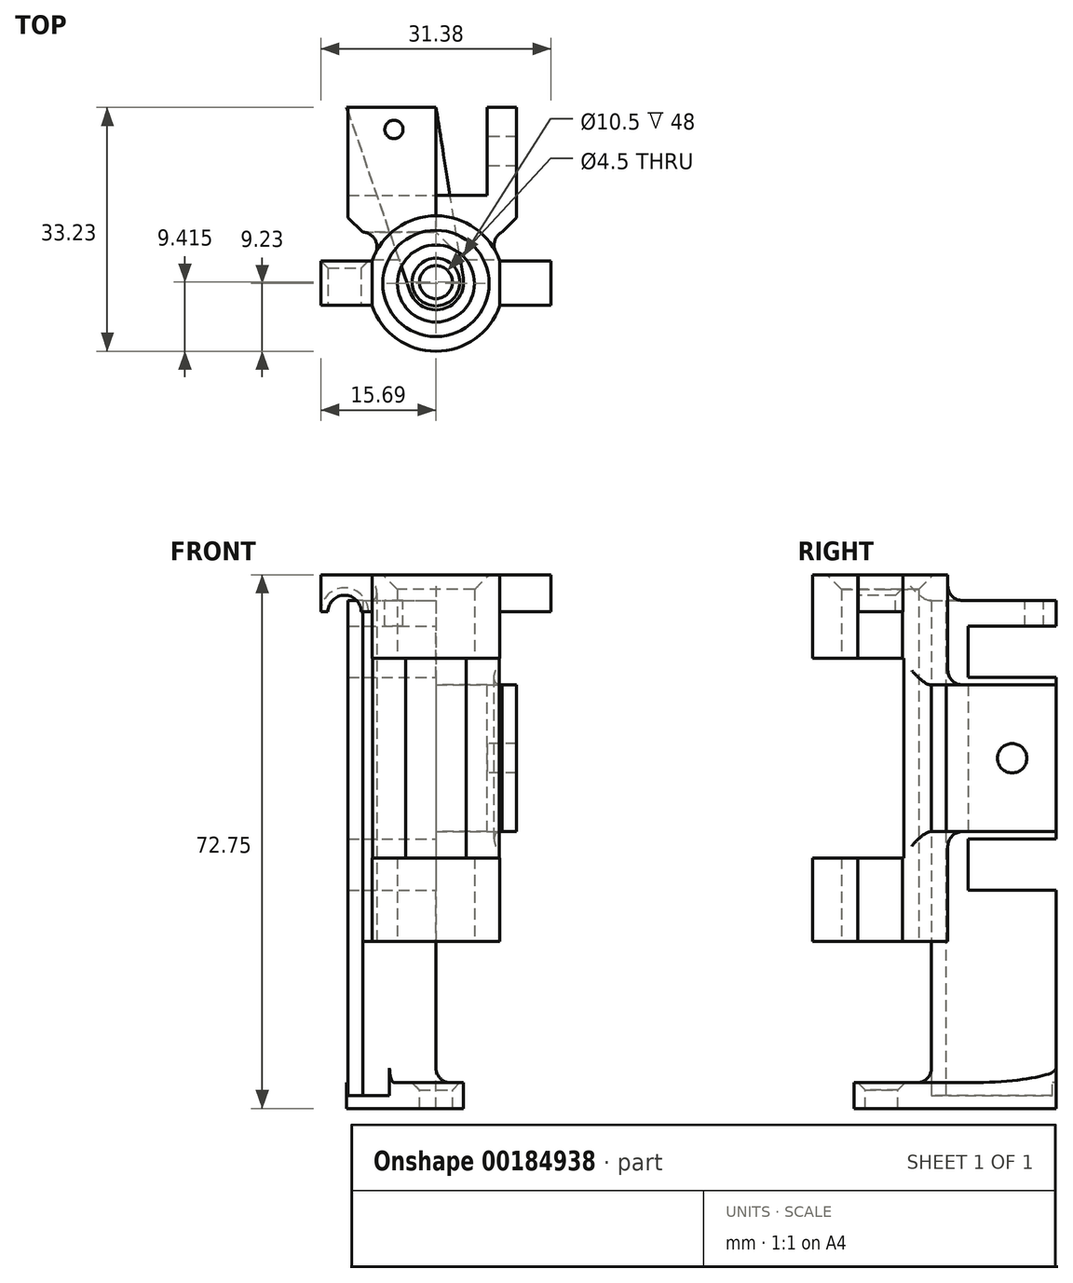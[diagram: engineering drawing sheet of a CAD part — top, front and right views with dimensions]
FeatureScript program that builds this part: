
annotation { "Feature Type Name" : "Feature", "Feature Type Description" : "" }
export const myFeature = defineFeature(function(context is Context, id is Id, definition is map)
    precondition{}
    {
        {
            var Q0;
            Q0=qCreatedBy(makeId("Front.planeOp"),FACE);
            var sketch = newSketch(context, id + "F0", { "sketchPlane" : qUnion([Q0])});
            skLineSegment(sketch, "E0", {"start": v(-12, 18) * mm, "end": v(-12, 11) * mm});
            skLineSegment(sketch, "E1", {"start": v(-12, 11) * mm, "end": v(0, 11) * mm});
            skLineSegment(sketch, "E2", {"start": v(0, 11) * mm, "end": v(0, 0) * mm});
            skLineSegment(sketch, "E3", {"start": v(-12, 18) * mm, "end": v(7, 18) * mm});
            skLineSegment(sketch, "E4", {"start": v(7, 18) * mm, "end": v(7, 0) * mm});
            skLineSegment(sketch, "E5.MirrorCS", {"start": v(0, -11) * mm, "end": v(0, 0) * mm});
            skLineSegment(sketch, "E6.MirrorCS", {"start": v(-12, -11) * mm, "end": v(0, -11) * mm});
            skLineSegment(sketch, "E7.MirrorCS", {"start": v(-12, -18) * mm, "end": v(-12, -11) * mm});
            skLineSegment(sketch, "E8.MirrorCS", {"start": v(-12, -18) * mm, "end": v(7, -18) * mm});
            skLineSegment(sketch, "E9.MirrorCS", {"start": v(7, -18) * mm, "end": v(7, 0) * mm});
            skSolve(sketch);
        }
        {
            var Q0;
            Q0=makeQuery(id+"F0.imprint","IMPRINT",FACE,{"disambiguationData":[TD([[makeQuery(id+"F0.imprint","IMPRINT",EDGE,{"derivedFrom":sQuery(id+"F0.wireOp",EDGE,"E0")}),1.0]])]});
            extrude(context, id + "F1", {"entities" : qUnion([Q0]), "depth" : 12 * mm});
        }
        {
            var Q0;
            Q0=qCreatedBy(makeId("Front.planeOp"),FACE);
            cPlane(context, id + "F2", {"entities" : qUnion([Q0]), "cplaneType" : CPlaneType.OFFSET, "offset" : 17 * mm, "width" : 150 * mm, "height" : 150 * mm});
        }
        {
            var Q0;
            Q0=qCreatedBy(id+"F2.planeOp",FACE);
            var sketch = newSketch(context, id + "F3", { "sketchPlane" : qUnion([Q0])});
            skLineSegment(sketch, "E10.bottom", {"start": v(-12, 21.5) * mm, "end": v(0, 21.5) * mm});
            skLineSegment(sketch, "E10.left", {"start": v(-12, 21.5) * mm, "end": v(-12, -27.5) * mm});
            skLineSegment(sketch, "E10.right", {"start": v(0, 21.5) * mm, "end": v(0, 10) * mm});
            skLineSegment(sketch, "E11", {"start": v(0, 10) * mm, "end": v(11, 10) * mm});
            skLineSegment(sketch, "E12", {"start": v(11, 10) * mm, "end": v(11, 0) * mm});
            skLineSegment(sketch, "E13.MirrorCS", {"start": v(0, -10) * mm, "end": v(11, -10) * mm});
            skLineSegment(sketch, "E14.MirrorCS", {"start": v(11, -10) * mm, "end": v(11, 0) * mm});
            skLineSegment(sketch, "E15.trimOffspring", {"start": v(0, -10) * mm, "end": v(0, -21.5) * mm});
            skLineSegment(sketch, "E16", {"start": v(-12, -27.5) * mm, "end": v(-12, -46) * mm});
            skLineSegment(sketch, "E17", {"start": v(-12, -46) * mm, "end": v(0, -46) * mm});
            skLineSegment(sketch, "E18", {"start": v(0, -46) * mm, "end": v(0, -21.5) * mm});
            skSolve(sketch);
        }
        {
            var Q0;
            Q0=makeQuery(id+"F3.imprint","IMPRINT",FACE,{"disambiguationData":[TD([[makeQuery(id+"F3.imprint","IMPRINT",EDGE,{"derivedFrom":sQuery(id+"F3.wireOp",EDGE,"E10.bottom")}),-1.0]])]});
            extrude(context, id + "F4", {"entities" : qUnion([Q0]), "oppositeDirection" : true, "depth" : 17 * mm});
        }
        {
            var Q0;
            Q0=makeQuery(id+"F1.opExtrude","SWEPT_BODY",BODY,{"disambiguationData":[OSD([sQuery(id+"F0.wireOp",EDGE,"E0"),sQuery(id+"F0.wireOp",EDGE,"E1"),sQuery(id+"F0.wireOp",EDGE,"E2"),sQuery(id+"F0.wireOp",EDGE,"E3"),sQuery(id+"F0.wireOp",EDGE,"E4"),sQuery(id+"F0.wireOp",EDGE,"E5.MirrorCS"),sQuery(id+"F0.wireOp",EDGE,"E6.MirrorCS"),sQuery(id+"F0.wireOp",EDGE,"E7.MirrorCS"),sQuery(id+"F0.wireOp",EDGE,"E8.MirrorCS"),sQuery(id+"F0.wireOp",EDGE,"E9.MirrorCS")])]});
            var Q1;
            Q1=makeQuery(id+"F4.opExtrude","SWEPT_BODY",BODY,{"disambiguationData":[OSD([sQuery(id+"F3.wireOp",EDGE,"E10.bottom"),sQuery(id+"F3.wireOp",EDGE,"E10.top"),sQuery(id+"F3.wireOp",EDGE,"E10.left"),sQuery(id+"F3.wireOp",EDGE,"E10.right"),sQuery(id+"F3.wireOp",EDGE,"E11"),sQuery(id+"F3.wireOp",EDGE,"E12"),sQuery(id+"F3.wireOp",EDGE,"E13.MirrorCS"),sQuery(id+"F3.wireOp",EDGE,"E14.MirrorCS"),sQuery(id+"F3.wireOp",EDGE,"E15.trimOffspring")])]});
            booleanBodies(context, id + "F5", {"operationType" : BooleanOperationType.SUBTRACTION, "tools" : qUnion([Q0]), "targets" : qUnion([Q1])});
        }
        {
            var Q0;
            Q0=qCreatedBy(makeId("Right.planeOp"),FACE);
            var sketch = newSketch(context, id + "F6", { "sketchPlane" : qUnion([Q0])});
            skCircle(sketch, "E19", {"center": v(-6, 0) * mm, "radius": 2 * mm});
            skSolve(sketch);
        }
        {
            var Q0;
            Q0 = qSketchRegion(id + "F6", true);
            extrude(context, id + "F7", {"entities" : qUnion([Q0]), "operationType" : NewBodyOperationType.REMOVE, "endBound" : BoundingType.THROUGH_ALL, "depth" : 25 * mm});
        }
        {
            var Q0;
            Q0=qCreatedBy(makeId("Top.planeOp"),FACE);
            var sketch = newSketch(context, id + "F8", { "sketchPlane" : qUnion([Q0])});
            skCircle(sketch, "E20", {"center": v(0, -24) * mm, "radius": 5.25 * mm});
            skArc(sketch, "E21", {"start": v(8.7, -20.95) * mm, "mid": v(0, -14.77) * mm, "end": v(-8.7, -20.95) * mm});
            skArc(sketch, "E22.trimOffspring", {"start": v(-8.7, -27.05) * mm, "mid": v(0, -33.23) * mm, "end": v(8.7, -27.05) * mm});
            skLineSegment(sketch, "E23", {"start": v(-8.7, -20.95) * mm, "end": v(-8.7, -27.05) * mm});
            skLineSegment(sketch, "E24.MirrorCS", {"start": v(8.7, -20.95) * mm, "end": v(8.7, -27.05) * mm});
            skLineSegment(sketch, "E25.left", {"start": v(8.7, -20.95) * mm, "end": v(8.7, -27.15) * mm});
            skLineSegment(sketch, "E26.MirrorCS", {"start": v(-8.7, -20.95) * mm, "end": v(-8.7, -27.15) * mm});
            skSolve(sketch);
        }
        {
            var Q0;
            Q0=makeQuery(id+"F8.imprint","IMPRINT",FACE,{"disambiguationData":[TD([[makeQuery(id+"F8.imprint","IMPRINT",EDGE,{"derivedFrom":sQuery(id+"F8.wireOp",EDGE,"E20")}),-1.0]])]});
            extrude(context, id + "F9", {"entities" : qUnion([Q0]), "operationType" : NewBodyOperationType.ADD, "endBound" : BoundingType.SYMMETRIC, "depth" : 50 * mm});
        }
        {
            var Q0;
            Q0=makeQuery(id+"F4.opExtrude","CAP_EDGE",EDGE,{"disambiguationData":[OSD([sQuery(id+"F3.wireOp",EDGE,"E12"),sQuery(id+"F3.wireOp",EDGE,"E14.MirrorCS")])],"isStart":true});
            var Q1;
            Q1=makeQuery(id+"F4.opExtrude","CAP_EDGE",EDGE,{"disambiguationData":[OSD([sQuery(id+"F3.wireOp",EDGE,"E10.left")])],"isStart":true});
            chamfer(context, id + "F10", {"entities" : qUnion([Q0, Q1]), "width" : 2 * mm, "tangentPropagation" : true});
        }
        {
            var Q0;
            Q0=qCreatedBy(makeId("Right.planeOp"),FACE);
            var sketch = newSketch(context, id + "F11", { "sketchPlane" : qUnion([Q0])});
            skLineSegment(sketch, "E27", {"start": v(-20.74, 0) * mm, "end": v(-20.74, 13.6) * mm});
            skLineSegment(sketch, "E28", {"start": v(-20.74, 13.6) * mm, "end": v(-36.17, 13.6) * mm});
            skLineSegment(sketch, "E29", {"start": v(-36.17, 13.6) * mm, "end": v(-36.17, 0) * mm});
            skLineSegment(sketch, "E30.MirrorCS", {"start": v(-20.74, 0) * mm, "end": v(-20.74, -13.6) * mm});
            skLineSegment(sketch, "E31.MirrorCS", {"start": v(-20.74, -13.6) * mm, "end": v(-36.17, -13.6) * mm});
            skLineSegment(sketch, "E32.MirrorCS", {"start": v(-36.17, -13.6) * mm, "end": v(-36.17, 0) * mm});
            skSolve(sketch);
        }
        {
            var Q0;
            Q0=makeQuery(id+"F11.imprint","IMPRINT",FACE,{"disambiguationData":[TD([[makeQuery(id+"F11.imprint","IMPRINT",EDGE,{"derivedFrom":sQuery(id+"F11.wireOp",EDGE,"E27")}),1.0]])]});
            extrude(context, id + "F12", {"entities" : qUnion([Q0]), "operationType" : NewBodyOperationType.REMOVE, "endBound" : BoundingType.SYMMETRIC, "oppositeDirection" : true, "depth" : 25 * mm});
        }
        {
            var Q0;
            Q0=makeQuery(id+"F9.boolean.opBoolean","INTERSECT",EDGE,{"derivedFrom":[makeQuery(id+"F4.opExtrude","SWEPT_FACE",FACE,{"disambiguationData":[OSD([sQuery(id+"F3.wireOp",EDGE,"E11")])]}),makeQuery(id+"F9.opExtrude","SWEPT_FACE",FACE,{"disambiguationData":[OSD([sQuery(id+"F8.wireOp",EDGE,"E21")])]})]});
            var Q1;
            Q1=makeQuery(id+"F9.boolean.opBoolean","INTERSECT",EDGE,{"derivedFrom":[makeQuery(id+"F4.opExtrude","SWEPT_FACE",FACE,{"disambiguationData":[OSD([sQuery(id+"F3.wireOp",EDGE,"E10.bottom")])]}),makeQuery(id+"F9.opExtrude","SWEPT_FACE",FACE,{"disambiguationData":[OSD([sQuery(id+"F8.wireOp",EDGE,"E21")])]})]});
            var Q2;
            Q2=makeQuery(id+"F9.boolean.opBoolean","INTERSECT",EDGE,{"derivedFrom":[makeQuery(id+"F4.opExtrude","SWEPT_FACE",FACE,{"disambiguationData":[OSD([sQuery(id+"F3.wireOp",EDGE,"E13.MirrorCS")])]}),makeQuery(id+"F9.opExtrude","SWEPT_FACE",FACE,{"disambiguationData":[OSD([sQuery(id+"F8.wireOp",EDGE,"E21")])]})]});
            var Q3;
            Q3=makeQuery(id+"F9.boolean.opBoolean","INTERSECT",EDGE,{"disambiguationData":[OD(1.0)],"derivedFrom":[makeQuery(id+"F4.opExtrude","CAP_FACE",FACE,{"disambiguationData":[OSD([sQuery(id+"F3.wireOp",EDGE,"E10.bottom"),sQuery(id+"F3.wireOp",EDGE,"E10.left"),sQuery(id+"F3.wireOp",EDGE,"E10.right"),sQuery(id+"F3.wireOp",EDGE,"E11"),sQuery(id+"F3.wireOp",EDGE,"E12"),sQuery(id+"F3.wireOp",EDGE,"E13.MirrorCS"),sQuery(id+"F3.wireOp",EDGE,"E14.MirrorCS"),sQuery(id+"F3.wireOp",EDGE,"E15.trimOffspring"),sQuery(id+"F3.wireOp",EDGE,"E16"),sQuery(id+"F3.wireOp",EDGE,"E17"),sQuery(id+"F3.wireOp",EDGE,"E18")])],"isStart":true}),makeQuery(id+"F9.opExtrude","SWEPT_FACE",FACE,{"disambiguationData":[OSD([sQuery(id+"F8.wireOp",EDGE,"E21")])]})]});
            fillet(context, id + "F13", {"entities" : qUnion([Q0, Q1, Q2, Q3]), "radius" : 2 * mm, "tangentPropagation" : true, "allowEdgeOverflow" : false});
        }
        {
            var Q0;
            Q0=makeQuery(id+"F9.opExtrude","CAP_EDGE",EDGE,{"disambiguationData":[OSD([sQuery(id+"F8.wireOp",EDGE,"E20")])],"isStart":false});
            chamfer(context, id + "F14", {"entities" : qUnion([Q0]), "width" : 2 * mm, "tangentPropagation" : true});
        }
        {
            var Q0;
            Q0=makeQuery(id+"F4.opExtrude","SWEPT_FACE",FACE,{"disambiguationData":[OSD([sQuery(id+"F3.wireOp",EDGE,"E17")])]});
            cPlane(context, id + "F15", {"entities" : qUnion([Q0]), "cplaneType" : CPlaneType.OFFSET, "offset" : 0 * mm, "width" : 150 * mm, "height" : 150 * mm});
        }
        {
            var Q0;
            Q0=qCreatedBy(id+"F15.planeOp",FACE);
            var sketch = newSketch(context, id + "F16", { "sketchPlane" : qUnion([Q0])});
            skCircle(sketch, "E33", {"center": v(0, 23.82) * mm, "radius": 2.25 * mm});
            skCircle(sketch, "E34", {"center": v(0, 23.82) * mm, "radius": 3.77 * mm});
            skLineSegment(sketch, "E35", {"start": v(3.72, 23.22) * mm, "end": v(0, 0) * mm});
            skLineSegment(sketch, "E36", {"start": v(0, 0) * mm, "end": v(-12.17, 0) * mm});
            skLineSegment(sketch, "E37", {"start": v(-12.17, 0) * mm, "end": v(-3.57, 25.04) * mm});
            skSolve(sketch);
        }
        {
            var Q0;
            {var subQ0=sQuery(id+"F16.wireOp",EDGE,"E35");Q0=makeQuery(id+"F16.imprint","IMPRINT",FACE,{"disambiguationData":[TD([[makeQuery(id+"F16.imprint","IMPRINT",EDGE,{"derivedFrom":subQ0}),-1.0]])]});}
            var Q1;
            Q1=makeQuery(id+"F16.imprint","IMPRINT",FACE,{"disambiguationData":[TD([[makeQuery(id+"F16.imprint","IMPRINT",EDGE,{"derivedFrom":sQuery(id+"F16.wireOp",EDGE,"E33")}),-1.0]])]});
            extrude(context, id + "F17", {"entities" : qUnion([Q0, Q1]), "endBound" : BoundingType.SYMMETRIC, "depth" : 3.5 * mm});
        }
        {
            var Q0;
            Q0=makeQuery(id+"F4.opExtrude","SWEPT_BODY",BODY,{"disambiguationData":[OSD([sQuery(id+"F3.wireOp",EDGE,"E10.bottom"),sQuery(id+"F3.wireOp",EDGE,"E10.left"),sQuery(id+"F3.wireOp",EDGE,"E10.right"),sQuery(id+"F3.wireOp",EDGE,"E11"),sQuery(id+"F3.wireOp",EDGE,"E12"),sQuery(id+"F3.wireOp",EDGE,"E13.MirrorCS"),sQuery(id+"F3.wireOp",EDGE,"E14.MirrorCS"),sQuery(id+"F3.wireOp",EDGE,"E15.trimOffspring"),sQuery(id+"F3.wireOp",EDGE,"E16"),sQuery(id+"F3.wireOp",EDGE,"E17"),sQuery(id+"F3.wireOp",EDGE,"E18")])]});
            var Q1;
            Q1=makeQuery(id+"F17.opExtrude","SWEPT_BODY",BODY,{"disambiguationData":[OSD([sQuery(id+"F16.wireOp",EDGE,"E33"),sQuery(id+"F16.wireOp",EDGE,"E34"),sQuery(id+"F16.wireOp",EDGE,"E35"),sQuery(id+"F16.wireOp",EDGE,"E36"),sQuery(id+"F16.wireOp",EDGE,"E37")])]});
            booleanBodies(context, id + "F18", {"operationType" : BooleanOperationType.UNION, "tools" : qUnion([Q0, Q1])});
        }
        {
            var Q0;
            Q0=makeQuery(id+"F4.opExtrude","SWEPT_FACE",FACE,{"disambiguationData":[OSD([sQuery(id+"F3.wireOp",EDGE,"E10.bottom")])]});
            var sketch = newSketch(context, id + "F19", { "sketchPlane" : qUnion([Q0])});
            skCircle(sketch, "E38", {"center": v(-5.73, -3) * mm, "radius": 1.25 * mm});
            skSolve(sketch);
        }
        {
            var Q0;
            Q0=makeQuery(id+"F19.imprint","IMPRINT",FACE,{"disambiguationData":[TD([[makeQuery(id+"F19.imprint","IMPRINT",EDGE,{"derivedFrom":sQuery(id+"F19.wireOp",EDGE,"E38")}),1.0]])]});
            extrude(context, id + "F20", {"entities" : qUnion([Q0]), "operationType" : NewBodyOperationType.REMOVE, "endBound" : BoundingType.UP_TO_NEXT, "oppositeDirection" : true, "depth" : 25 * mm});
        }
        {
            var Q0;
            Q0=makeQuery(id+"F17.opExtrude","CAP_EDGE",EDGE,{"disambiguationData":[OSD([sQuery(id+"F16.wireOp",EDGE,"E33")])],"isStart":true});
            chamfer(context, id + "F21", {"entities" : qUnion([Q0]), "width" : 1 * mm, "tangentPropagation" : true});
        }
        {
            var Q0;
            {var subQ0=sQuery(id+"F3.wireOp",EDGE,"E10.right");var subQ2=sQuery(id+"F3.wireOp",EDGE,"E16");var subQ3=sQuery(id+"F3.wireOp",EDGE,"E10.left");var subQ4=sQuery(id+"F3.wireOp",EDGE,"E10.bottom");var subQ5=sQuery(id+"F3.wireOp",EDGE,"E17");var subQ6=sQuery(id+"F3.wireOp",EDGE,"E18");var subQ7=sQuery(id+"F3.wireOp",EDGE,"E15.trimOffspring");Q0=makeQuery(id+"F18.opBoolean","INTERSECT",EDGE,{"derivedFrom":[makeQuery(id+"F9.boolean.opBoolean","SPLIT",FACE,{"disambiguationData":[TD([makeQuery(id+"F4.opExtrude","SWEPT_FACE",FACE,{"disambiguationData":[OSD([subQ4])]})])],"derivedFrom":makeQuery(id+"F4.opExtrude","CAP_FACE",FACE,{"disambiguationData":[OSD([subQ4,subQ3,subQ0,sQuery(id+"F3.wireOp",EDGE,"E11"),sQuery(id+"F3.wireOp",EDGE,"E12"),sQuery(id+"F3.wireOp",EDGE,"E13.MirrorCS"),sQuery(id+"F3.wireOp",EDGE,"E14.MirrorCS"),subQ7,subQ2,subQ5,subQ6])],"isStart":true})}),makeQuery(id+"F17.opExtrude","CAP_FACE",FACE,{"disambiguationData":[OSD([sQuery(id+"F16.wireOp",EDGE,"E33"),sQuery(id+"F16.wireOp",EDGE,"E34"),sQuery(id+"F16.wireOp",EDGE,"E35"),sQuery(id+"F16.wireOp",EDGE,"E36"),sQuery(id+"F16.wireOp",EDGE,"E37")])],"isStart":true})]});}
            var Q1;
            Q1=makeQuery(id+"F18.opBoolean","INTERSECT",EDGE,{"derivedFrom":[makeQuery(id+"F5.opBoolean","MERGE",FACE,{"derivedFrom":[makeQuery(id+"F1.opExtrude","SWEPT_FACE",FACE,{"disambiguationData":[OSD([sQuery(id+"F0.wireOp",EDGE,"E2"),sQuery(id+"F0.wireOp",EDGE,"E5.MirrorCS")])]}),makeQuery(id+"F4.opExtrude","SWEPT_FACE",FACE,{"disambiguationData":[OSD([sQuery(id+"F3.wireOp",EDGE,"E10.right")])]}),makeQuery(id+"F4.opExtrude","SWEPT_FACE",FACE,{"disambiguationData":[OSD([sQuery(id+"F3.wireOp",EDGE,"E15.trimOffspring"),sQuery(id+"F3.wireOp",EDGE,"E18")])]})]}),makeQuery(id+"F17.opExtrude","CAP_FACE",FACE,{"disambiguationData":[OSD([sQuery(id+"F16.wireOp",EDGE,"E33"),sQuery(id+"F16.wireOp",EDGE,"E34"),sQuery(id+"F16.wireOp",EDGE,"E35"),sQuery(id+"F16.wireOp",EDGE,"E36"),sQuery(id+"F16.wireOp",EDGE,"E37")])],"isStart":true})]});
            fillet(context, id + "F22", {"entities" : qUnion([Q0, Q1]), "radius" : 2 * mm, "tangentPropagation" : true, "allowEdgeOverflow" : false});
        }
        {
            var Q0;
            Q0=makeQuery(id+"F9.opExtrude","CAP_FACE",FACE,{"disambiguationData":[OSD([sQuery(id+"F8.wireOp",EDGE,"E20"),sQuery(id+"F8.wireOp",EDGE,"E21"),sQuery(id+"F8.wireOp",EDGE,"E22.trimOffspring"),sQuery(id+"F8.wireOp",EDGE,"E25.left"),sQuery(id+"F8.wireOp",EDGE,"E26.MirrorCS")])],"isStart":false});
            cPlane(context, id + "F23", {"entities" : qUnion([Q0]), "cplaneType" : CPlaneType.OFFSET, "offset" : 0 * mm, "width" : 150 * mm, "height" : 150 * mm});
        }
        {
            var Q0;
            Q0=qCreatedBy(id+"F23.planeOp",FACE);
            var sketch = newSketch(context, id + "F24", { "sketchPlane" : qUnion([Q0])});
            skLineSegment(sketch, "E39.bottom", {"start": v(8.7, -20.9) * mm, "end": v(15.7, -20.9) * mm});
            skLineSegment(sketch, "E39.top", {"start": v(8.7, -26.97) * mm, "end": v(15.7, -26.97) * mm});
            skLineSegment(sketch, "E39.left", {"start": v(8.7, -20.9) * mm, "end": v(8.7, -26.97) * mm});
            skLineSegment(sketch, "E39.right", {"start": v(15.7, -20.9) * mm, "end": v(15.7, -26.97) * mm});
            skLineSegment(sketch, "E40.MirrorCS", {"start": v(-8.7, -20.9) * mm, "end": v(-15.7, -20.9) * mm});
            skLineSegment(sketch, "E41.MirrorCS", {"start": v(-15.7, -20.9) * mm, "end": v(-15.7, -26.97) * mm});
            skLineSegment(sketch, "E42.MirrorCS", {"start": v(-8.7, -26.97) * mm, "end": v(-15.7, -26.97) * mm});
            skLineSegment(sketch, "E43.MirrorCS", {"start": v(-8.7, -20.9) * mm, "end": v(-8.7, -26.97) * mm});
            skLineSegment(sketch, "E44.bottom", {"start": v(-15.7, -20.9) * mm, "end": v(-13.2, -20.9) * mm});
            skLineSegment(sketch, "E44.top", {"start": v(-15.7, -26.97) * mm, "end": v(-12.2, -26.97) * mm});
            skLineSegment(sketch, "E45.MirrorCS", {"start": v(15.7, -26.97) * mm, "end": v(12.2, -26.97) * mm});
            skLineSegment(sketch, "E46.MirrorCS", {"start": v(15.7, -20.9) * mm, "end": v(13.2, -20.9) * mm});
            skSolve(sketch);
        }
        {
            var Q0;
            Q0=makeQuery(id+"F24.imprint","IMPRINT",FACE,{"disambiguationData":[TD([[makeQuery(id+"F24.imprint","IMPRINT",EDGE,{"derivedFrom":sQuery(id+"F24.wireOp",EDGE,"E40.MirrorCS")}),1.0]])]});
            var Q1;
            Q1=makeQuery(id+"F24.imprint","IMPRINT",FACE,{"disambiguationData":[TD([[makeQuery(id+"F24.imprint","IMPRINT",EDGE,{"derivedFrom":sQuery(id+"F24.wireOp",EDGE,"E39.bottom")}),-1.0]])]});
            extrude(context, id + "F25", {"entities" : qUnion([Q0, Q1]), "oppositeDirection" : true, "depth" : 5 * mm});
        }
        {
            var Q0;
            Q0=makeQuery(id+"F25.opExtrude","SWEPT_FACE",FACE,{"disambiguationData":[OSD([sQuery(id+"F24.wireOp",EDGE,"E42.MirrorCS"),sQuery(id+"F24.wireOp",EDGE,"E44.top")])]});
            cPlane(context, id + "F26", {"entities" : qUnion([Q0]), "cplaneType" : CPlaneType.OFFSET, "offset" : 0 * mm, "width" : 150 * mm, "height" : 150 * mm});
        }
        {
            var Q0;
            Q0=qCreatedBy(id+"F26.planeOp",FACE);
            var sketch = newSketch(context, id + "F27", { "sketchPlane" : qUnion([Q0])});
            skCircle(sketch, "E47", {"center": v(-12.46, 19.97) * mm, "radius": 2.26 * mm});
            skCircle(sketch, "E48.MirrorC", {"center": v(12.46, 19.97) * mm, "radius": 2.26 * mm});
            skSolve(sketch);
        }
        {
            var Q0;
            Q0=makeQuery(id+"F27.imprint","IMPRINT",FACE,{"disambiguationData":[TD([[makeQuery(id+"F27.imprint","IMPRINT",EDGE,{"derivedFrom":sQuery(id+"F27.wireOp",EDGE,"E47")}),1.0]])]});
            var Q1;
            Q1=makeQuery(id+"F27.imprint","IMPRINT",FACE,{"disambiguationData":[TD([[makeQuery(id+"F27.imprint","IMPRINT",EDGE,{"derivedFrom":sQuery(id+"F27.wireOp",EDGE,"E48.MirrorC")}),-1.0]])]});
            var Q2;
            Q2=sQuery(id+"F27.wireOp",EDGE,"E47");
            var Q3;
            Q3=sQuery(id+"F27.wireOp",EDGE,"E48.MirrorC");
            extrude(context, id + "F28", {"entities" : qUnion([Q0, Q1]), "operationType" : NewBodyOperationType.REMOVE, "surfaceEntities" : qUnion([Q2, Q3]), "oppositeDirection" : true, "depth" : 8 * mm});
        }
        {
            var Q0;
            Q0=makeQuery(id+"F28.boolean.opBoolean","COPY",EDGE,{"derivedFrom":makeQuery(id+"F28.opExtrude","CAP_EDGE",EDGE,{"disambiguationData":[OSD([sQuery(id+"F27.wireOp",EDGE,"E47")])],"isStart":true})});
            var Q1;
            Q1=makeQuery(id+"F28.boolean.opBoolean","COPY",EDGE,{"derivedFrom":makeQuery(id+"F28.opExtrude","CAP_EDGE",EDGE,{"disambiguationData":[OSD([sQuery(id+"F27.wireOp",EDGE,"E48.MirrorC")])],"isStart":true})});
            var Q2;
            Q2=makeQuery(id+"F28.boolean.opBoolean","INTERSECT",EDGE,{"derivedFrom":[makeQuery(id+"F25.opExtrude","SWEPT_FACE",FACE,{"disambiguationData":[OSD([sQuery(id+"F24.wireOp",EDGE,"E39.bottom"),sQuery(id+"F24.wireOp",EDGE,"E46.MirrorCS")])]}),makeQuery(id+"F28.opExtrude","SWEPT_FACE",FACE,{"disambiguationData":[OSD([sQuery(id+"F27.wireOp",EDGE,"E48.MirrorC")])]})]});
            var Q3;
            Q3=makeQuery(id+"F28.boolean.opBoolean","INTERSECT",EDGE,{"derivedFrom":[makeQuery(id+"F25.opExtrude","SWEPT_FACE",FACE,{"disambiguationData":[OSD([sQuery(id+"F24.wireOp",EDGE,"E40.MirrorCS"),sQuery(id+"F24.wireOp",EDGE,"E44.bottom")])]}),makeQuery(id+"F28.opExtrude","SWEPT_FACE",FACE,{"disambiguationData":[OSD([sQuery(id+"F27.wireOp",EDGE,"E47")])]})]});
            chamfer(context, id + "F29", {"entities" : qUnion([Q0, Q1, Q2, Q3]), "width" : 1 * mm, "tangentPropagation" : true});
        }
    });
